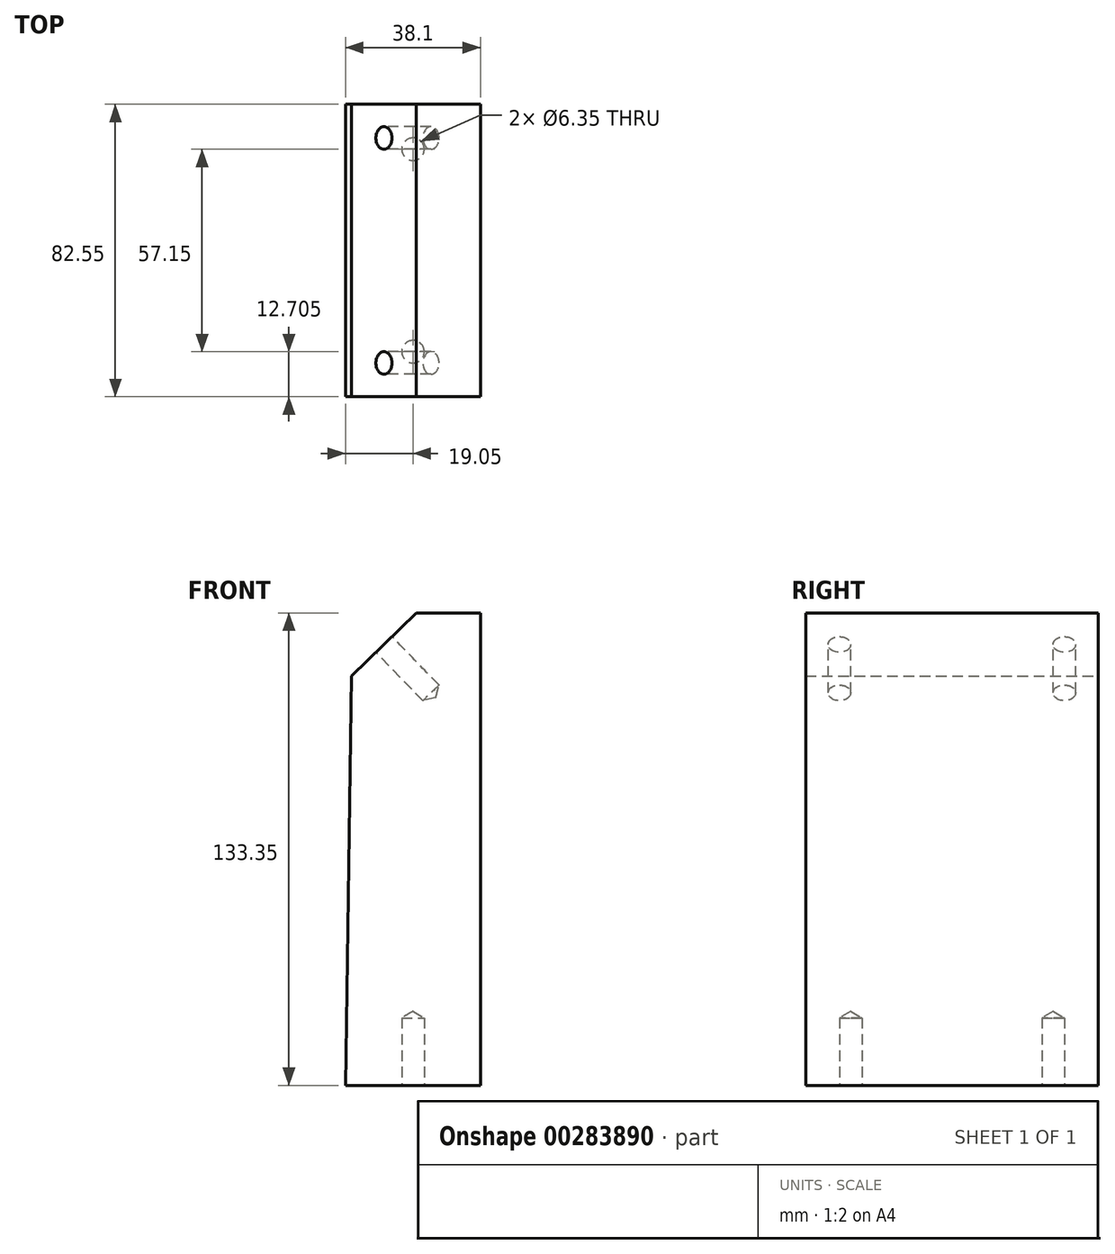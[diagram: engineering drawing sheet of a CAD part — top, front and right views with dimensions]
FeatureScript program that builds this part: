
annotation { "Feature Type Name" : "Feature", "Feature Type Description" : "" }
export const myFeature = defineFeature(function(context is Context, id is Id, definition is map)
    precondition{}
    {
        {
            var Q0;
            Q0=qCreatedBy(makeId("Front.planeOp"),FACE);
            var sketch = newSketch(context, id + "F0", { "sketchPlane" : qUnion([Q0])});
            skLineSegment(sketch, "E0.bottom", {"start": v(0, 0) * mm, "end": v(38.1, 0) * mm});
            skLineSegment(sketch, "E0.top", {"start": v(20.02, 133.35) * mm, "end": v(38.1, 133.35) * mm});
            skLineSegment(sketch, "E0.left", {"start": v(0, 0) * mm, "end": v(1.67, 115.53) * mm});
            skLineSegment(sketch, "E1", {"start": v(20.02, 133.35) * mm, "end": v(1.67, 115.53) * mm});
            skPoint(sketch, "E2.orphan", {"position": v(1.93, 133.35) * mm});
            skLineSegment(sketch, "E3", {"start": v(38.1, 133.35) * mm, "end": v(38.1, 0) * mm});
            skSolve(sketch);
        }
        {
            var Q0;
            Q0 = qSketchRegion(id + "F0", true);
            extrude(context, id + "F1", {"entities" : qUnion([Q0]), "depth" : 76.2 * mm});
        }
        {
            var Q0;
            Q0=makeQuery(id+"F1.opExtrude","SWEPT_FACE",FACE,{"disambiguationData":[OSD([sQuery(id+"F0.wireOp",EDGE,"E1")])]});
            var sketch = newSketch(context, id + "F2", { "sketchPlane" : qUnion([Q0])});
            skPoint(sketch, "E4", {"position": v(94.49, -6.35) * mm});
            skPoint(sketch, "E4.positionSnap0", {"position": v(94.49, 0) * mm});
            skPoint(sketch, "E5", {"position": v(94.49, -69.85) * mm});
            skSolve(sketch);
        }
        {
            var Q0;
            Q0=sQuery(id+"F2.wireOp",VERTEX,"E4");
            var Q1;
            Q1=sQuery(id+"F2.wireOp",VERTEX,"E5");
            var Q2;
            Q2=makeQuery(id+"F1.opExtrude","SWEPT_BODY",BODY,{"disambiguationData":[OSD([sQuery(id+"F0.wireOp",EDGE,"E0.bottom"),sQuery(id+"F0.wireOp",EDGE,"E0.top"),sQuery(id+"F0.wireOp",EDGE,"E0.left"),sQuery(id+"F0.wireOp",EDGE,"E1"),sQuery(id+"F0.wireOp",EDGE,"E3")])]});
            hole(context, id + "F3", {"style" : HoleStyle.SIMPLE, "endStyle" : HoleEndStyle.BLIND, "holeDiameter" : 6.35 * mm, "holeDepth" : 19.05 * mm, "tappedDepth" : 12.7 * mm, "tapClearance" : 3, "locations" : qUnion([Q0, Q1]), "scope" : qUnion([Q2])});
        }
        {
            var Q0;
            Q0=makeQuery(id+"F1.opExtrude","CAP_FACE",FACE,{"disambiguationData":[OSD([sQuery(id+"F0.wireOp",EDGE,"E0.bottom"),sQuery(id+"F0.wireOp",EDGE,"E0.top"),sQuery(id+"F0.wireOp",EDGE,"E0.left"),sQuery(id+"F0.wireOp",EDGE,"E1"),sQuery(id+"F0.wireOp",EDGE,"E3")])],"isStart":false});
            var sketch = newSketch(context, id + "F4", { "sketchPlane" : qUnion([Q0])});
            skSolve(sketch);
        }
        {
            var Q0;
            Q0 = qSketchRegion(id + "F4", true);
            var Q1;
            Q1=makeQuery(id+"F4.imprint","IMPRINT",FACE,{"disambiguationData":[TD([[makeQuery(id+"F4.imprint","IMPRINT",EDGE,{"derivedFrom":makeQuery(id+"F1.opExtrude","CAP_EDGE",EDGE,{"disambiguationData":[OSD([sQuery(id+"F0.wireOp",EDGE,"E0.bottom")])],"isStart":false})}),1.0]])]});
            extrude(context, id + "F5", {"entities" : qUnion([Q0, Q1]), "operationType" : NewBodyOperationType.ADD, "depth" : 3.17 * mm});
        }
        {
            var Q0;
            Q0=makeQuery(id+"F1.opExtrude","CAP_FACE",FACE,{"disambiguationData":[OSD([sQuery(id+"F0.wireOp",EDGE,"E0.bottom"),sQuery(id+"F0.wireOp",EDGE,"E0.top"),sQuery(id+"F0.wireOp",EDGE,"E0.left"),sQuery(id+"F0.wireOp",EDGE,"E1"),sQuery(id+"F0.wireOp",EDGE,"E3")])],"isStart":true});
            var sketch = newSketch(context, id + "F6", { "sketchPlane" : qUnion([Q0])});
            skSolve(sketch);
        }
        {
            var Q0;
            Q0 = qSketchRegion(id + "F6", true);
            var Q1;
            Q1=makeQuery(id+"F6.imprint","IMPRINT",FACE,{"disambiguationData":[TD([[makeQuery(id+"F6.imprint","IMPRINT",EDGE,{"derivedFrom":makeQuery(id+"F1.opExtrude","CAP_EDGE",EDGE,{"disambiguationData":[OSD([sQuery(id+"F0.wireOp",EDGE,"E0.bottom")])],"isStart":true})}),-1.0]])]});
            extrude(context, id + "F7", {"entities" : qUnion([Q0, Q1]), "operationType" : NewBodyOperationType.ADD, "depth" : 3.17 * mm});
        }
        {
            var Q0;
            {var subQ0=sQuery(id+"F0.wireOp",EDGE,"E0.bottom");Q0=makeQuery(id+"F7.boolean.opBoolean","MERGE",FACE,{"derivedFrom":[makeQuery(id+"F5.boolean.opBoolean","MERGE",FACE,{"derivedFrom":[makeQuery(id+"F1.opExtrude","SWEPT_FACE",FACE,{"disambiguationData":[OSD([subQ0])]}),makeQuery(id+"F5.opExtrude","SWEPT_FACE",FACE,{"disambiguationData":[OSD([subQ0])]})]}),makeQuery(id+"F7.opExtrude","SWEPT_FACE",FACE,{"disambiguationData":[OSD([subQ0])]})]});}
            var sketch = newSketch(context, id + "F8", { "sketchPlane" : qUnion([Q0])});
            skPoint(sketch, "E6", {"position": v(19.05, 9.53) * mm});
            skPoint(sketch, "E6.positionSnap0", {"position": v(19.05, -3.18) * mm});
            skPoint(sketch, "E7", {"position": v(19.05, 66.67) * mm});
            skPoint(sketch, "E7.positionSnap0", {"position": v(19.05, 79.38) * mm});
            skSolve(sketch);
        }
        {
            var Q0;
            Q0=sQuery(id+"F8.wireOp",VERTEX,"E6");
            var Q1;
            Q1=sQuery(id+"F8.wireOp",VERTEX,"E7");
            var Q2;
            Q2=makeQuery(id+"F1.opExtrude","SWEPT_BODY",BODY,{"disambiguationData":[OSD([sQuery(id+"F0.wireOp",EDGE,"E0.bottom"),sQuery(id+"F0.wireOp",EDGE,"E0.top"),sQuery(id+"F0.wireOp",EDGE,"E0.left"),sQuery(id+"F0.wireOp",EDGE,"E1"),sQuery(id+"F0.wireOp",EDGE,"E3")])]});
            hole(context, id + "F9", {"style" : HoleStyle.SIMPLE, "endStyle" : HoleEndStyle.BLIND, "holeDiameter" : 6.35 * mm, "holeDepth" : 19.05 * mm, "tappedDepth" : 12.7 * mm, "tapClearance" : 3, "locations" : qUnion([Q0, Q1]), "scope" : qUnion([Q2])});
        }
    });
